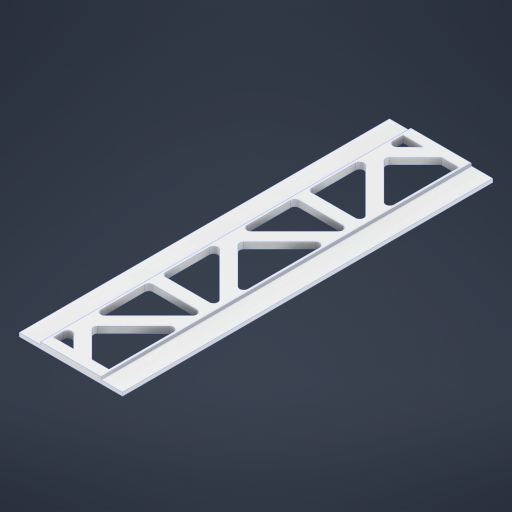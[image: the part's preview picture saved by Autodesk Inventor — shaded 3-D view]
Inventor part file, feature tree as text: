
AUTODESK INVENTOR PART (.ipt)
format: ipt  version: 2024 (Build 280153000, 153)  size: 450,560 bytes
history: native  units: mm
features: extrude x6, sketch x6, projected_geometry x2, other x1, fillet x1
ambient origin geometry x8: Origin, YZ Plane, XZ Plane, XY Plane, X Axis, Y Axis, Z Axis, Center Point
bodies: Body1 (feature_tree)
feature tree (16):
  other  "Твердое тело1"
  extrude  "Выдавливание1"  Depth=140.0mm
  extrude  "Выдавливание2"  Depth=12.0mm
  extrude  "Выдавливание4"  Depth=5.0mm TaperAngle=0.0deg
  extrude  "Extrusion6"  Depth=5.0mm
  fillet  "Fillet2"  [1 undecoded]
  extrude  "Extrusion7"  TaperAngle=90.0deg  [1 undecoded]
  extrude  "Extrusion8"  TaperAngle=90.0deg  [1 undecoded]
  sketch  "Эскиз1"
  sketch  "Эскиз2"
  projected_geometry  "Спроецированная петля1"
  sketch  "Эскиз3"
  projected_geometry  "Спроецированная петля2"
  sketch  "Sketch5"  dims[d0=777.0mm d1=140.0mm]
  sketch  "Sketch6"  dims[d2=12.0mm d3=0.0mm d4=12.0mm]
  sketch  "Sketch7"  dims[d5=12.0mm d6=5.0mm d7=0.0mm d8=5.0mm d11=90.0deg d12=90.0deg d13=90.0deg d15=90.0deg d16=90.0deg d17=108.5mm d18=45.0deg d22=25.0mm d25=23.0mm d26=0.0mm d34=25.0mm d35=25.0mm d38=23.0mm d39=0.0mm d40=8.0mm d41=41.0mm d42=41.0mm d43=33.5mm d44=33.5mm d45=30.0mm d46=0.0mm d47=20.0mm d48=20.0mm d49=30.0mm d50=0.0mm d30=0.5mm d31=0.872665mm d32=0.5mm d33=0.872665mm]
note: 3 required parameter values undecoded (feature->parameter linkage not recoverable at this tier; creation-order binding heuristic only, values carry confidence <= 0.55)
